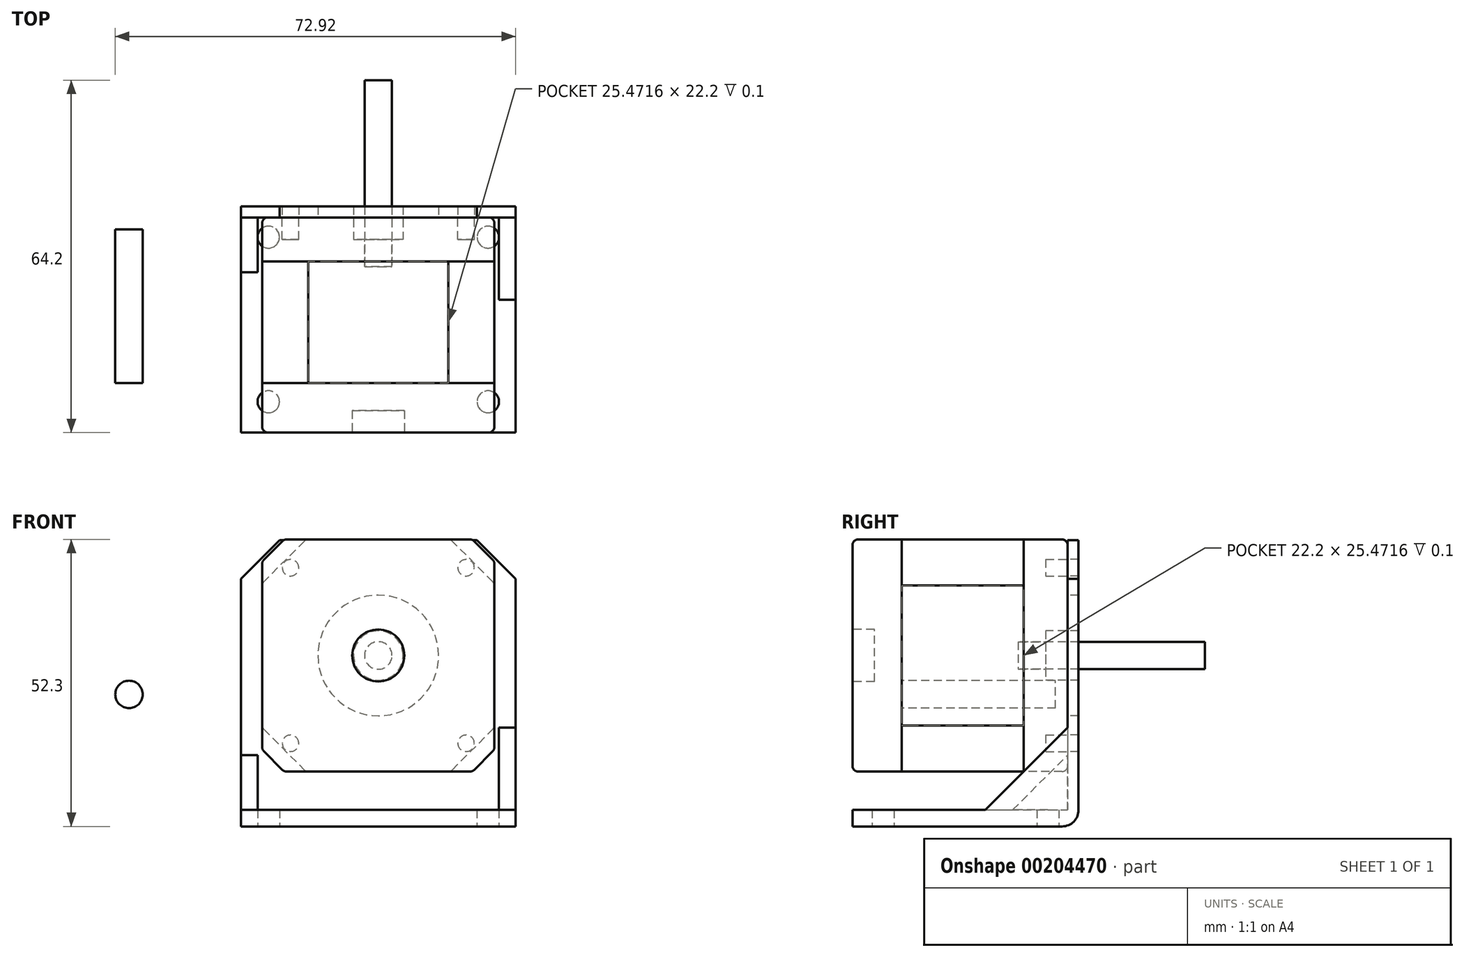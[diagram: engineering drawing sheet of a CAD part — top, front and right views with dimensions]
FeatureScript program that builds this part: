
annotation { "Feature Type Name" : "Feature", "Feature Type Description" : "" }
export const myFeature = defineFeature(function(context is Context, id is Id, definition is map)
    precondition{}
    {
        {
            var Q0;
            Q0=qCreatedBy(makeId("Front.planeOp"),FACE);
            var sketch = newSketch(context, id + "F0", { "sketchPlane" : qUnion([Q0])});
            skLineSegment(sketch, "E0.bottom", {"start": v(-21.15, 21.15) * mm, "end": v(21.15, 21.15) * mm});
            skLineSegment(sketch, "E0.top", {"start": v(-21.15, -21.15) * mm, "end": v(21.15, -21.15) * mm});
            skLineSegment(sketch, "E0.left", {"start": v(-21.15, 21.15) * mm, "end": v(-21.15, -21.15) * mm});
            skLineSegment(sketch, "E0.right", {"start": v(21.15, 21.15) * mm, "end": v(21.15, -21.15) * mm});
            skSolve(sketch);
        }
        {
            var Q0;
            Q0=makeQuery(id+"F0.imprint","IMPRINT",FACE,{"disambiguationData":[TD([[makeQuery(id+"F0.imprint","IMPRINT",EDGE,{"derivedFrom":sQuery(id+"F0.wireOp",EDGE,"E0.bottom")}),-1.0]])]});
            extrude(context, id + "F1", {"entities" : qUnion([Q0]), "depth" : 9 * mm});
        }
        {
            var Q0;
            Q0=makeQuery(id+"F1.opExtrude","CAP_FACE",FACE,{"disambiguationData":[OSD([sQuery(id+"F0.wireOp",EDGE,"E0.bottom"),sQuery(id+"F0.wireOp",EDGE,"E0.top"),sQuery(id+"F0.wireOp",EDGE,"E0.left"),sQuery(id+"F0.wireOp",EDGE,"E0.right")])],"isStart":true});
            var sketch = newSketch(context, id + "F2", { "sketchPlane" : qUnion([Q0])});
            skLineSegment(sketch, "E1.bottom", {"start": v(-21.15, 21.15) * mm, "end": v(21.15, 21.15) * mm});
            skLineSegment(sketch, "E1.top", {"start": v(-21.15, -21.15) * mm, "end": v(21.15, -21.15) * mm});
            skLineSegment(sketch, "E1.left", {"start": v(-21.15, 21.15) * mm, "end": v(-21.15, -21.15) * mm});
            skLineSegment(sketch, "E1.right", {"start": v(21.15, 21.15) * mm, "end": v(21.15, -21.15) * mm});
            skPoint(sketch, "E2", {"position": v(-13.15, 21.15) * mm});
            skPoint(sketch, "E3", {"position": v(-21.15, 13.15) * mm});
            skLineSegment(sketch, "E4", {"start": v(-21.15, 13.15) * mm, "end": v(-13.15, 21.15) * mm});
            skLineSegment(sketch, "E5.1.0", {"start": v(-13.15, -21.15) * mm, "end": v(-21.15, -13.15) * mm});
            skLineSegment(sketch, "E5.2.0", {"start": v(21.15, -13.15) * mm, "end": v(13.15, -21.15) * mm});
            skLineSegment(sketch, "E5.3.0", {"start": v(13.15, 21.15) * mm, "end": v(21.15, 13.15) * mm});
            skPoint(sketch, "E5.center", {"position": v(0, 0) * mm});
            skSolve(sketch);
        }
        {
            var Q0;
            Q0=makeQuery(id+"F1.opExtrude","SWEPT_EDGE",EDGE,{"disambiguationData":[OSD([sQuery(id+"F0.wireOp",EDGE,"E0.bottom"),sQuery(id+"F0.wireOp",EDGE,"E0.right")])]});
            var Q1;
            Q1=makeQuery(id+"F1.opExtrude","SWEPT_EDGE",EDGE,{"disambiguationData":[OSD([sQuery(id+"F0.wireOp",EDGE,"E0.bottom"),sQuery(id+"F0.wireOp",EDGE,"E0.left")])]});
            var Q2;
            Q2=makeQuery(id+"F1.opExtrude","SWEPT_EDGE",EDGE,{"disambiguationData":[OSD([sQuery(id+"F0.wireOp",EDGE,"E0.top"),sQuery(id+"F0.wireOp",EDGE,"E0.right")])]});
            var Q3;
            Q3=makeQuery(id+"F1.opExtrude","SWEPT_EDGE",EDGE,{"disambiguationData":[OSD([sQuery(id+"F0.wireOp",EDGE,"E0.top"),sQuery(id+"F0.wireOp",EDGE,"E0.left")])]});
            chamfer(context, id + "F3", {"entities" : qUnion([Q0, Q1, Q2, Q3]), "width" : 4 * mm, "tangentPropagation" : true});
        }
        {
            var Q0;
            {var subQ0=sQuery(id+"F0.wireOp",EDGE,"E0.bottom");Q0=makeQuery(id+"F3.opChamfer","BLEND_EDGE",EDGE,{"blendedFrom":[makeQuery(id+"F1.opExtrude","SWEPT_EDGE",EDGE,{"disambiguationData":[OSD([subQ0,sQuery(id+"F0.wireOp",EDGE,"E0.right")])]}),makeQuery(id+"F1.opExtrude","SWEPT_FACE",FACE,{"disambiguationData":[OSD([subQ0])]})],"blendedInto":[makeQuery(id+"F1.opExtrude","SWEPT_FACE",FACE,{"disambiguationData":[OSD([subQ0])]})]});}
            var Q1;
            {var subQ0=sQuery(id+"F0.wireOp",EDGE,"E0.right");Q1=makeQuery(id+"F3.opChamfer","BLEND_EDGE",EDGE,{"blendedFrom":[makeQuery(id+"F1.opExtrude","SWEPT_EDGE",EDGE,{"disambiguationData":[OSD([sQuery(id+"F0.wireOp",EDGE,"E0.bottom"),subQ0])]}),makeQuery(id+"F1.opExtrude","SWEPT_FACE",FACE,{"disambiguationData":[OSD([subQ0])]})],"blendedInto":[makeQuery(id+"F1.opExtrude","SWEPT_FACE",FACE,{"disambiguationData":[OSD([subQ0])]})]});}
            var Q2;
            {var subQ0=sQuery(id+"F0.wireOp",EDGE,"E0.bottom");Q2=makeQuery(id+"F3.opChamfer","BLEND_EDGE",EDGE,{"blendedFrom":[makeQuery(id+"F1.opExtrude","SWEPT_EDGE",EDGE,{"disambiguationData":[OSD([subQ0,sQuery(id+"F0.wireOp",EDGE,"E0.left")])]}),makeQuery(id+"F1.opExtrude","SWEPT_FACE",FACE,{"disambiguationData":[OSD([subQ0])]})],"blendedInto":[makeQuery(id+"F1.opExtrude","SWEPT_FACE",FACE,{"disambiguationData":[OSD([subQ0])]})]});}
            var Q3;
            {var subQ0=sQuery(id+"F0.wireOp",EDGE,"E0.right");Q3=makeQuery(id+"F3.opChamfer","BLEND_EDGE",EDGE,{"blendedFrom":[makeQuery(id+"F1.opExtrude","SWEPT_EDGE",EDGE,{"disambiguationData":[OSD([sQuery(id+"F0.wireOp",EDGE,"E0.top"),subQ0])]}),makeQuery(id+"F1.opExtrude","SWEPT_FACE",FACE,{"disambiguationData":[OSD([subQ0])]})],"blendedInto":[makeQuery(id+"F1.opExtrude","SWEPT_FACE",FACE,{"disambiguationData":[OSD([subQ0])]})]});}
            var Q4;
            {var subQ0=sQuery(id+"F0.wireOp",EDGE,"E0.top");Q4=makeQuery(id+"F3.opChamfer","BLEND_EDGE",EDGE,{"blendedFrom":[makeQuery(id+"F1.opExtrude","SWEPT_EDGE",EDGE,{"disambiguationData":[OSD([subQ0,sQuery(id+"F0.wireOp",EDGE,"E0.right")])]}),makeQuery(id+"F1.opExtrude","SWEPT_FACE",FACE,{"disambiguationData":[OSD([subQ0])]})],"blendedInto":[makeQuery(id+"F1.opExtrude","SWEPT_FACE",FACE,{"disambiguationData":[OSD([subQ0])]})]});}
            var Q5;
            {var subQ0=sQuery(id+"F0.wireOp",EDGE,"E0.left");Q5=makeQuery(id+"F3.opChamfer","BLEND_EDGE",EDGE,{"blendedFrom":[makeQuery(id+"F1.opExtrude","SWEPT_EDGE",EDGE,{"disambiguationData":[OSD([sQuery(id+"F0.wireOp",EDGE,"E0.bottom"),subQ0])]}),makeQuery(id+"F1.opExtrude","SWEPT_FACE",FACE,{"disambiguationData":[OSD([subQ0])]})],"blendedInto":[makeQuery(id+"F1.opExtrude","SWEPT_FACE",FACE,{"disambiguationData":[OSD([subQ0])]})]});}
            var Q6;
            {var subQ0=sQuery(id+"F0.wireOp",EDGE,"E0.left");Q6=makeQuery(id+"F3.opChamfer","BLEND_EDGE",EDGE,{"blendedFrom":[makeQuery(id+"F1.opExtrude","SWEPT_EDGE",EDGE,{"disambiguationData":[OSD([sQuery(id+"F0.wireOp",EDGE,"E0.top"),subQ0])]}),makeQuery(id+"F1.opExtrude","SWEPT_FACE",FACE,{"disambiguationData":[OSD([subQ0])]})],"blendedInto":[makeQuery(id+"F1.opExtrude","SWEPT_FACE",FACE,{"disambiguationData":[OSD([subQ0])]})]});}
            var Q7;
            {var subQ0=sQuery(id+"F0.wireOp",EDGE,"E0.top");Q7=makeQuery(id+"F3.opChamfer","BLEND_EDGE",EDGE,{"blendedFrom":[makeQuery(id+"F1.opExtrude","SWEPT_EDGE",EDGE,{"disambiguationData":[OSD([subQ0,sQuery(id+"F0.wireOp",EDGE,"E0.left")])]}),makeQuery(id+"F1.opExtrude","SWEPT_FACE",FACE,{"disambiguationData":[OSD([subQ0])]})],"blendedInto":[makeQuery(id+"F1.opExtrude","SWEPT_FACE",FACE,{"disambiguationData":[OSD([subQ0])]})]});}
            fillet(context, id + "F4", {"entities" : qUnion([Q0, Q1, Q2, Q3, Q4, Q5, Q6, Q7]), "radius" : 1 * mm, "tangentPropagation" : true, "allowEdgeOverflow" : false});
        }
        {
            var Q0;
            {var subQ0=sQuery(id+"F2.wireOp",EDGE,"E4");Q0=makeQuery(id+"F2.imprint","IMPRINT",FACE,{"disambiguationData":[TD([[makeQuery(id+"F2.imprint","IMPRINT",EDGE,{"derivedFrom":subQ0}),-1.0]])]});}
            extrude(context, id + "F5", {"entities" : qUnion([Q0]), "operationType" : NewBodyOperationType.ADD, "depth" : 22.2 * mm});
        }
        {
            var Q0;
            Q0=makeQuery(id+"F5.opExtrude","CAP_FACE",FACE,{"disambiguationData":[OSD([sQuery(id+"F2.wireOp",EDGE,"E1.bottom"),sQuery(id+"F2.wireOp",EDGE,"E1.top"),sQuery(id+"F2.wireOp",EDGE,"E1.left"),sQuery(id+"F2.wireOp",EDGE,"E1.right"),sQuery(id+"F2.wireOp",EDGE,"E4"),sQuery(id+"F2.wireOp",EDGE,"E5.1.0"),sQuery(id+"F2.wireOp",EDGE,"E5.2.0"),sQuery(id+"F2.wireOp",EDGE,"E5.3.0")])],"isStart":false});
            var sketch = newSketch(context, id + "F6", { "sketchPlane" : qUnion([Q0])});
            skLineSegment(sketch, "E6.bottom", {"start": v(-21.15, 21.15) * mm, "end": v(21.15, 21.15) * mm});
            skLineSegment(sketch, "E6.top", {"start": v(-21.15, -21.15) * mm, "end": v(21.15, -21.15) * mm});
            skLineSegment(sketch, "E6.left", {"start": v(-21.15, 21.15) * mm, "end": v(-21.15, -21.15) * mm});
            skLineSegment(sketch, "E6.right", {"start": v(21.15, 21.15) * mm, "end": v(21.15, -21.15) * mm});
            skSolve(sketch);
        }
        {
            var Q0;
            Q0=qSketchRegion(id+"F6",true);
            extrude(context, id + "F7", {"entities" : qUnion([Q0]), "operationType" : NewBodyOperationType.ADD, "depth" : 8 * mm});
        }
        {
            var Q0;
            Q0=makeQuery(id+"F7.opExtrude","SWEPT_EDGE",EDGE,{"disambiguationData":[OSD([sQuery(id+"F6.wireOp",EDGE,"E6.bottom"),sQuery(id+"F6.wireOp",EDGE,"E6.left")])]});
            var Q1;
            Q1=makeQuery(id+"F7.opExtrude","SWEPT_EDGE",EDGE,{"disambiguationData":[OSD([sQuery(id+"F6.wireOp",EDGE,"E6.bottom"),sQuery(id+"F6.wireOp",EDGE,"E6.right")])]});
            var Q2;
            Q2=makeQuery(id+"F7.opExtrude","SWEPT_EDGE",EDGE,{"disambiguationData":[OSD([sQuery(id+"F6.wireOp",EDGE,"E6.top"),sQuery(id+"F6.wireOp",EDGE,"E6.left")])]});
            var Q3;
            Q3=makeQuery(id+"F7.opExtrude","SWEPT_EDGE",EDGE,{"disambiguationData":[OSD([sQuery(id+"F6.wireOp",EDGE,"E6.top"),sQuery(id+"F6.wireOp",EDGE,"E6.right")])]});
            chamfer(context, id + "F8", {"entities" : qUnion([Q0, Q1, Q2, Q3]), "width" : 4 * mm, "tangentPropagation" : true});
        }
        {
            var Q0;
            Q0=makeQuery(id+"F1.opExtrude","CAP_EDGE",EDGE,{"disambiguationData":[OSD([sQuery(id+"F0.wireOp",EDGE,"E0.right")])],"isStart":false});
            var Q1;
            Q1=makeQuery(id+"F5.opExtrude","SWEPT_EDGE",EDGE,{"disambiguationData":[OSD([sQuery(id+"F2.wireOp",EDGE,"E1.left"),sQuery(id+"F2.wireOp",EDGE,"E4")])]});
            var Q2;
            Q2=makeQuery(id+"F5.opExtrude","SWEPT_EDGE",EDGE,{"disambiguationData":[OSD([sQuery(id+"F2.wireOp",EDGE,"E1.bottom"),sQuery(id+"F2.wireOp",EDGE,"E4")])]});
            var Q3;
            {var subQ0=sQuery(id+"F6.wireOp",EDGE,"E6.left");Q3=makeQuery(id+"F8.opChamfer","BLEND_EDGE",EDGE,{"blendedFrom":[makeQuery(id+"F7.opExtrude","SWEPT_EDGE",EDGE,{"disambiguationData":[OSD([sQuery(id+"F6.wireOp",EDGE,"E6.bottom"),subQ0])]}),makeQuery(id+"F7.boolean.opBoolean","MERGE",FACE,{"derivedFrom":[makeQuery(id+"F5.boolean.opBoolean","MERGE",FACE,{"derivedFrom":[makeQuery(id+"F1.opExtrude","SWEPT_FACE",FACE,{"disambiguationData":[OSD([sQuery(id+"F0.wireOp",EDGE,"E0.right")])]}),makeQuery(id+"F5.opExtrude","SWEPT_FACE",FACE,{"disambiguationData":[OSD([sQuery(id+"F2.wireOp",EDGE,"E1.left")])]})]}),makeQuery(id+"F7.opExtrude","SWEPT_FACE",FACE,{"disambiguationData":[OSD([subQ0])]})]})],"blendedInto":[makeQuery(id+"F7.boolean.opBoolean","MERGE",FACE,{"derivedFrom":[makeQuery(id+"F5.boolean.opBoolean","MERGE",FACE,{"derivedFrom":[makeQuery(id+"F1.opExtrude","SWEPT_FACE",FACE,{"disambiguationData":[OSD([sQuery(id+"F0.wireOp",EDGE,"E0.right")])]}),makeQuery(id+"F5.opExtrude","SWEPT_FACE",FACE,{"disambiguationData":[OSD([sQuery(id+"F2.wireOp",EDGE,"E1.left")])]})]}),makeQuery(id+"F7.opExtrude","SWEPT_FACE",FACE,{"disambiguationData":[OSD([subQ0])]})]})]});}
            var Q4;
            {var subQ0=sQuery(id+"F6.wireOp",EDGE,"E6.bottom");Q4=makeQuery(id+"F8.opChamfer","BLEND_EDGE",EDGE,{"blendedFrom":[makeQuery(id+"F7.opExtrude","SWEPT_EDGE",EDGE,{"disambiguationData":[OSD([subQ0,sQuery(id+"F6.wireOp",EDGE,"E6.left")])]}),makeQuery(id+"F7.boolean.opBoolean","MERGE",FACE,{"derivedFrom":[makeQuery(id+"F5.boolean.opBoolean","MERGE",FACE,{"derivedFrom":[makeQuery(id+"F1.opExtrude","SWEPT_FACE",FACE,{"disambiguationData":[OSD([sQuery(id+"F0.wireOp",EDGE,"E0.bottom")])]}),makeQuery(id+"F5.opExtrude","SWEPT_FACE",FACE,{"disambiguationData":[OSD([sQuery(id+"F2.wireOp",EDGE,"E1.bottom")])]})]}),makeQuery(id+"F7.opExtrude","SWEPT_FACE",FACE,{"disambiguationData":[OSD([subQ0])]})]})],"blendedInto":[makeQuery(id+"F7.boolean.opBoolean","MERGE",FACE,{"derivedFrom":[makeQuery(id+"F5.boolean.opBoolean","MERGE",FACE,{"derivedFrom":[makeQuery(id+"F1.opExtrude","SWEPT_FACE",FACE,{"disambiguationData":[OSD([sQuery(id+"F0.wireOp",EDGE,"E0.bottom")])]}),makeQuery(id+"F5.opExtrude","SWEPT_FACE",FACE,{"disambiguationData":[OSD([sQuery(id+"F2.wireOp",EDGE,"E1.bottom")])]})]}),makeQuery(id+"F7.opExtrude","SWEPT_FACE",FACE,{"disambiguationData":[OSD([subQ0])]})]})]});}
            var Q5;
            {var subQ0=sQuery(id+"F6.wireOp",EDGE,"E6.bottom");Q5=makeQuery(id+"F8.opChamfer","BLEND_EDGE",EDGE,{"blendedFrom":[makeQuery(id+"F7.opExtrude","SWEPT_EDGE",EDGE,{"disambiguationData":[OSD([subQ0,sQuery(id+"F6.wireOp",EDGE,"E6.right")])]}),makeQuery(id+"F7.boolean.opBoolean","MERGE",FACE,{"derivedFrom":[makeQuery(id+"F5.boolean.opBoolean","MERGE",FACE,{"derivedFrom":[makeQuery(id+"F1.opExtrude","SWEPT_FACE",FACE,{"disambiguationData":[OSD([sQuery(id+"F0.wireOp",EDGE,"E0.bottom")])]}),makeQuery(id+"F5.opExtrude","SWEPT_FACE",FACE,{"disambiguationData":[OSD([sQuery(id+"F2.wireOp",EDGE,"E1.bottom")])]})]}),makeQuery(id+"F7.opExtrude","SWEPT_FACE",FACE,{"disambiguationData":[OSD([subQ0])]})]})],"blendedInto":[makeQuery(id+"F7.boolean.opBoolean","MERGE",FACE,{"derivedFrom":[makeQuery(id+"F5.boolean.opBoolean","MERGE",FACE,{"derivedFrom":[makeQuery(id+"F1.opExtrude","SWEPT_FACE",FACE,{"disambiguationData":[OSD([sQuery(id+"F0.wireOp",EDGE,"E0.bottom")])]}),makeQuery(id+"F5.opExtrude","SWEPT_FACE",FACE,{"disambiguationData":[OSD([sQuery(id+"F2.wireOp",EDGE,"E1.bottom")])]})]}),makeQuery(id+"F7.opExtrude","SWEPT_FACE",FACE,{"disambiguationData":[OSD([subQ0])]})]})]});}
            var Q6;
            Q6=makeQuery(id+"F5.opExtrude","SWEPT_EDGE",EDGE,{"disambiguationData":[OSD([sQuery(id+"F2.wireOp",EDGE,"E1.bottom"),sQuery(id+"F2.wireOp",EDGE,"E5.3.0")])]});
            var Q7;
            {var subQ0=sQuery(id+"F6.wireOp",EDGE,"E6.right");Q7=makeQuery(id+"F8.opChamfer","BLEND_EDGE",EDGE,{"blendedFrom":[makeQuery(id+"F7.opExtrude","SWEPT_EDGE",EDGE,{"disambiguationData":[OSD([sQuery(id+"F6.wireOp",EDGE,"E6.bottom"),subQ0])]}),makeQuery(id+"F7.boolean.opBoolean","MERGE",FACE,{"derivedFrom":[makeQuery(id+"F5.boolean.opBoolean","MERGE",FACE,{"derivedFrom":[makeQuery(id+"F1.opExtrude","SWEPT_FACE",FACE,{"disambiguationData":[OSD([sQuery(id+"F0.wireOp",EDGE,"E0.left")])]}),makeQuery(id+"F5.opExtrude","SWEPT_FACE",FACE,{"disambiguationData":[OSD([sQuery(id+"F2.wireOp",EDGE,"E1.right")])]})]}),makeQuery(id+"F7.opExtrude","SWEPT_FACE",FACE,{"disambiguationData":[OSD([subQ0])]})]})],"blendedInto":[makeQuery(id+"F7.boolean.opBoolean","MERGE",FACE,{"derivedFrom":[makeQuery(id+"F5.boolean.opBoolean","MERGE",FACE,{"derivedFrom":[makeQuery(id+"F1.opExtrude","SWEPT_FACE",FACE,{"disambiguationData":[OSD([sQuery(id+"F0.wireOp",EDGE,"E0.left")])]}),makeQuery(id+"F5.opExtrude","SWEPT_FACE",FACE,{"disambiguationData":[OSD([sQuery(id+"F2.wireOp",EDGE,"E1.right")])]})]}),makeQuery(id+"F7.opExtrude","SWEPT_FACE",FACE,{"disambiguationData":[OSD([subQ0])]})]})]});}
            var Q8;
            Q8=makeQuery(id+"F5.opExtrude","SWEPT_EDGE",EDGE,{"disambiguationData":[OSD([sQuery(id+"F2.wireOp",EDGE,"E1.right"),sQuery(id+"F2.wireOp",EDGE,"E5.3.0")])]});
            var Q9;
            Q9=makeQuery(id+"F5.opExtrude","SWEPT_EDGE",EDGE,{"disambiguationData":[OSD([sQuery(id+"F2.wireOp",EDGE,"E1.right"),sQuery(id+"F2.wireOp",EDGE,"E5.2.0")])]});
            var Q10;
            {var subQ0=sQuery(id+"F6.wireOp",EDGE,"E6.right");Q10=makeQuery(id+"F8.opChamfer","BLEND_EDGE",EDGE,{"blendedFrom":[makeQuery(id+"F7.opExtrude","SWEPT_EDGE",EDGE,{"disambiguationData":[OSD([sQuery(id+"F6.wireOp",EDGE,"E6.top"),subQ0])]}),makeQuery(id+"F7.boolean.opBoolean","MERGE",FACE,{"derivedFrom":[makeQuery(id+"F5.boolean.opBoolean","MERGE",FACE,{"derivedFrom":[makeQuery(id+"F1.opExtrude","SWEPT_FACE",FACE,{"disambiguationData":[OSD([sQuery(id+"F0.wireOp",EDGE,"E0.left")])]}),makeQuery(id+"F5.opExtrude","SWEPT_FACE",FACE,{"disambiguationData":[OSD([sQuery(id+"F2.wireOp",EDGE,"E1.right")])]})]}),makeQuery(id+"F7.opExtrude","SWEPT_FACE",FACE,{"disambiguationData":[OSD([subQ0])]})]})],"blendedInto":[makeQuery(id+"F7.boolean.opBoolean","MERGE",FACE,{"derivedFrom":[makeQuery(id+"F5.boolean.opBoolean","MERGE",FACE,{"derivedFrom":[makeQuery(id+"F1.opExtrude","SWEPT_FACE",FACE,{"disambiguationData":[OSD([sQuery(id+"F0.wireOp",EDGE,"E0.left")])]}),makeQuery(id+"F5.opExtrude","SWEPT_FACE",FACE,{"disambiguationData":[OSD([sQuery(id+"F2.wireOp",EDGE,"E1.right")])]})]}),makeQuery(id+"F7.opExtrude","SWEPT_FACE",FACE,{"disambiguationData":[OSD([subQ0])]})]})]});}
            var Q11;
            {var subQ0=sQuery(id+"F6.wireOp",EDGE,"E6.top");Q11=makeQuery(id+"F8.opChamfer","BLEND_EDGE",EDGE,{"blendedFrom":[makeQuery(id+"F7.opExtrude","SWEPT_EDGE",EDGE,{"disambiguationData":[OSD([subQ0,sQuery(id+"F6.wireOp",EDGE,"E6.right")])]}),makeQuery(id+"F7.boolean.opBoolean","MERGE",FACE,{"derivedFrom":[makeQuery(id+"F5.boolean.opBoolean","MERGE",FACE,{"derivedFrom":[makeQuery(id+"F1.opExtrude","SWEPT_FACE",FACE,{"disambiguationData":[OSD([sQuery(id+"F0.wireOp",EDGE,"E0.top")])]}),makeQuery(id+"F5.opExtrude","SWEPT_FACE",FACE,{"disambiguationData":[OSD([sQuery(id+"F2.wireOp",EDGE,"E1.top")])]})]}),makeQuery(id+"F7.opExtrude","SWEPT_FACE",FACE,{"disambiguationData":[OSD([subQ0])]})]})],"blendedInto":[makeQuery(id+"F7.boolean.opBoolean","MERGE",FACE,{"derivedFrom":[makeQuery(id+"F5.boolean.opBoolean","MERGE",FACE,{"derivedFrom":[makeQuery(id+"F1.opExtrude","SWEPT_FACE",FACE,{"disambiguationData":[OSD([sQuery(id+"F0.wireOp",EDGE,"E0.top")])]}),makeQuery(id+"F5.opExtrude","SWEPT_FACE",FACE,{"disambiguationData":[OSD([sQuery(id+"F2.wireOp",EDGE,"E1.top")])]})]}),makeQuery(id+"F7.opExtrude","SWEPT_FACE",FACE,{"disambiguationData":[OSD([subQ0])]})]})]});}
            var Q12;
            Q12=makeQuery(id+"F5.opExtrude","SWEPT_EDGE",EDGE,{"disambiguationData":[OSD([sQuery(id+"F2.wireOp",EDGE,"E1.top"),sQuery(id+"F2.wireOp",EDGE,"E5.2.0")])]});
            var Q13;
            Q13=makeQuery(id+"F5.opExtrude","SWEPT_EDGE",EDGE,{"disambiguationData":[OSD([sQuery(id+"F2.wireOp",EDGE,"E1.top"),sQuery(id+"F2.wireOp",EDGE,"E5.1.0")])]});
            var Q14;
            {var subQ0=sQuery(id+"F6.wireOp",EDGE,"E6.top");Q14=makeQuery(id+"F8.opChamfer","BLEND_EDGE",EDGE,{"blendedFrom":[makeQuery(id+"F7.opExtrude","SWEPT_EDGE",EDGE,{"disambiguationData":[OSD([subQ0,sQuery(id+"F6.wireOp",EDGE,"E6.left")])]}),makeQuery(id+"F7.boolean.opBoolean","MERGE",FACE,{"derivedFrom":[makeQuery(id+"F5.boolean.opBoolean","MERGE",FACE,{"derivedFrom":[makeQuery(id+"F1.opExtrude","SWEPT_FACE",FACE,{"disambiguationData":[OSD([sQuery(id+"F0.wireOp",EDGE,"E0.top")])]}),makeQuery(id+"F5.opExtrude","SWEPT_FACE",FACE,{"disambiguationData":[OSD([sQuery(id+"F2.wireOp",EDGE,"E1.top")])]})]}),makeQuery(id+"F7.opExtrude","SWEPT_FACE",FACE,{"disambiguationData":[OSD([subQ0])]})]})],"blendedInto":[makeQuery(id+"F7.boolean.opBoolean","MERGE",FACE,{"derivedFrom":[makeQuery(id+"F5.boolean.opBoolean","MERGE",FACE,{"derivedFrom":[makeQuery(id+"F1.opExtrude","SWEPT_FACE",FACE,{"disambiguationData":[OSD([sQuery(id+"F0.wireOp",EDGE,"E0.top")])]}),makeQuery(id+"F5.opExtrude","SWEPT_FACE",FACE,{"disambiguationData":[OSD([sQuery(id+"F2.wireOp",EDGE,"E1.top")])]})]}),makeQuery(id+"F7.opExtrude","SWEPT_FACE",FACE,{"disambiguationData":[OSD([subQ0])]})]})]});}
            var Q15;
            {var subQ0=sQuery(id+"F6.wireOp",EDGE,"E6.left");Q15=makeQuery(id+"F8.opChamfer","BLEND_EDGE",EDGE,{"blendedFrom":[makeQuery(id+"F7.opExtrude","SWEPT_EDGE",EDGE,{"disambiguationData":[OSD([sQuery(id+"F6.wireOp",EDGE,"E6.top"),subQ0])]}),makeQuery(id+"F7.boolean.opBoolean","MERGE",FACE,{"derivedFrom":[makeQuery(id+"F5.boolean.opBoolean","MERGE",FACE,{"derivedFrom":[makeQuery(id+"F1.opExtrude","SWEPT_FACE",FACE,{"disambiguationData":[OSD([sQuery(id+"F0.wireOp",EDGE,"E0.right")])]}),makeQuery(id+"F5.opExtrude","SWEPT_FACE",FACE,{"disambiguationData":[OSD([sQuery(id+"F2.wireOp",EDGE,"E1.left")])]})]}),makeQuery(id+"F7.opExtrude","SWEPT_FACE",FACE,{"disambiguationData":[OSD([subQ0])]})]})],"blendedInto":[makeQuery(id+"F7.boolean.opBoolean","MERGE",FACE,{"derivedFrom":[makeQuery(id+"F5.boolean.opBoolean","MERGE",FACE,{"derivedFrom":[makeQuery(id+"F1.opExtrude","SWEPT_FACE",FACE,{"disambiguationData":[OSD([sQuery(id+"F0.wireOp",EDGE,"E0.right")])]}),makeQuery(id+"F5.opExtrude","SWEPT_FACE",FACE,{"disambiguationData":[OSD([sQuery(id+"F2.wireOp",EDGE,"E1.left")])]})]}),makeQuery(id+"F7.opExtrude","SWEPT_FACE",FACE,{"disambiguationData":[OSD([subQ0])]})]})]});}
            var Q16;
            Q16=makeQuery(id+"F5.opExtrude","SWEPT_EDGE",EDGE,{"disambiguationData":[OSD([sQuery(id+"F2.wireOp",EDGE,"E1.left"),sQuery(id+"F2.wireOp",EDGE,"E5.1.0")])]});
            var Q17;
            Q17=makeQuery(id+"F7.opExtrude","CAP_EDGE",EDGE,{"disambiguationData":[OSD([sQuery(id+"F6.wireOp",EDGE,"E6.bottom")])],"isStart":false});
            var Q18;
            Q18=makeQuery(id+"F7.opExtrude","CAP_FACE",FACE,{"disambiguationData":[OSD([sQuery(id+"F6.wireOp",EDGE,"E6.bottom"),sQuery(id+"F6.wireOp",EDGE,"E6.top"),sQuery(id+"F6.wireOp",EDGE,"E6.left"),sQuery(id+"F6.wireOp",EDGE,"E6.right")])],"isStart":false});
            fillet(context, id + "F9", {"entities" : qUnion([Q0, Q1, Q2, Q3, Q4, Q5, Q6, Q7, Q8, Q9, Q10, Q11, Q12, Q13, Q14, Q15, Q16, Q17, Q18]), "radius" : 1 * mm, "tangentPropagation" : true, "allowEdgeOverflow" : false});
        }
        {
            var Q0;
            Q0=makeQuery(id+"F7.boolean.opBoolean","MERGE",FACE,{"derivedFrom":[makeQuery(id+"F5.boolean.opBoolean","MERGE",FACE,{"derivedFrom":[makeQuery(id+"F1.opExtrude","SWEPT_FACE",FACE,{"disambiguationData":[OSD([sQuery(id+"F0.wireOp",EDGE,"E0.right")])]}),makeQuery(id+"F5.opExtrude","SWEPT_FACE",FACE,{"disambiguationData":[OSD([sQuery(id+"F2.wireOp",EDGE,"E1.left")])]})]}),makeQuery(id+"F7.opExtrude","SWEPT_FACE",FACE,{"disambiguationData":[OSD([sQuery(id+"F6.wireOp",EDGE,"E6.left")])]})]});
            var sketch = newSketch(context, id + "F10", { "sketchPlane" : qUnion([Q0])});
            skLineSegment(sketch, "E7", {"start": v(0, 12.74) * mm, "end": v(0, -12.74) * mm});
            skLineSegment(sketch, "E8", {"start": v(22.2, 12.74) * mm, "end": v(22.2, -12.74) * mm});
            skSolve(sketch);
        }
        {
            var Q0;
            Q0=makeQuery(id+"F10.imprint","IMPRINT",FACE,{"disambiguationData":[TD([[makeQuery(id+"F10.imprint","IMPRINT",EDGE,{"derivedFrom":sQuery(id+"F10.wireOp",EDGE,"E7")}),1.0]])]});
            extrude(context, id + "F11", {"entities" : qUnion([Q0]), "operationType" : NewBodyOperationType.REMOVE, "oppositeDirection" : true, "depth" : 0.1 * mm});
        }
        {
            var Q0;
            Q0=makeQuery(id+"F7.boolean.opBoolean","MERGE",FACE,{"derivedFrom":[makeQuery(id+"F5.boolean.opBoolean","MERGE",FACE,{"derivedFrom":[makeQuery(id+"F1.opExtrude","SWEPT_FACE",FACE,{"disambiguationData":[OSD([sQuery(id+"F0.wireOp",EDGE,"E0.bottom")])]}),makeQuery(id+"F5.opExtrude","SWEPT_FACE",FACE,{"disambiguationData":[OSD([sQuery(id+"F2.wireOp",EDGE,"E1.bottom")])]})]}),makeQuery(id+"F7.opExtrude","SWEPT_FACE",FACE,{"disambiguationData":[OSD([sQuery(id+"F6.wireOp",EDGE,"E6.bottom")])]})]});
            var sketch = newSketch(context, id + "F12", { "sketchPlane" : qUnion([Q0])});
            skLineSegment(sketch, "E9", {"start": v(12.74, 0) * mm, "end": v(-12.74, 0) * mm});
            skLineSegment(sketch, "E10", {"start": v(-12.74, 22.2) * mm, "end": v(12.74, 22.2) * mm});
            skSolve(sketch);
        }
        {
            var Q0;
            Q0=makeQuery(id+"F12.imprint","IMPRINT",FACE,{"disambiguationData":[TD([[makeQuery(id+"F12.imprint","IMPRINT",EDGE,{"derivedFrom":sQuery(id+"F12.wireOp",EDGE,"E9")}),-1.0]])]});
            extrude(context, id + "F13", {"entities" : qUnion([Q0]), "operationType" : NewBodyOperationType.REMOVE, "oppositeDirection" : true, "depth" : 0.1 * mm});
        }
        {
            var Q0;
            Q0=makeQuery(id+"F7.boolean.opBoolean","MERGE",FACE,{"derivedFrom":[makeQuery(id+"F5.boolean.opBoolean","MERGE",FACE,{"derivedFrom":[makeQuery(id+"F1.opExtrude","SWEPT_FACE",FACE,{"disambiguationData":[OSD([sQuery(id+"F0.wireOp",EDGE,"E0.left")])]}),makeQuery(id+"F5.opExtrude","SWEPT_FACE",FACE,{"disambiguationData":[OSD([sQuery(id+"F2.wireOp",EDGE,"E1.right")])]})]}),makeQuery(id+"F7.opExtrude","SWEPT_FACE",FACE,{"disambiguationData":[OSD([sQuery(id+"F6.wireOp",EDGE,"E6.right")])]})]});
            var sketch = newSketch(context, id + "F14", { "sketchPlane" : qUnion([Q0])});
            skLineSegment(sketch, "E11", {"start": v(0, 12.74) * mm, "end": v(0, -12.74) * mm});
            skLineSegment(sketch, "E12", {"start": v(-22.2, 12.74) * mm, "end": v(-22.2, -12.74) * mm});
            skSolve(sketch);
        }
        {
            var Q0;
            Q0=makeQuery(id+"F14.imprint","IMPRINT",FACE,{"disambiguationData":[TD([[makeQuery(id+"F14.imprint","IMPRINT",EDGE,{"derivedFrom":sQuery(id+"F14.wireOp",EDGE,"E11")}),-1.0]])]});
            extrude(context, id + "F15", {"entities" : qUnion([Q0]), "operationType" : NewBodyOperationType.REMOVE, "oppositeDirection" : true, "depth" : 0.1 * mm});
        }
        {
            var Q0;
            Q0=makeQuery(id+"F7.boolean.opBoolean","MERGE",FACE,{"derivedFrom":[makeQuery(id+"F5.boolean.opBoolean","MERGE",FACE,{"derivedFrom":[makeQuery(id+"F1.opExtrude","SWEPT_FACE",FACE,{"disambiguationData":[OSD([sQuery(id+"F0.wireOp",EDGE,"E0.top")])]}),makeQuery(id+"F5.opExtrude","SWEPT_FACE",FACE,{"disambiguationData":[OSD([sQuery(id+"F2.wireOp",EDGE,"E1.top")])]})]}),makeQuery(id+"F7.opExtrude","SWEPT_FACE",FACE,{"disambiguationData":[OSD([sQuery(id+"F6.wireOp",EDGE,"E6.top")])]})]});
            var sketch = newSketch(context, id + "F16", { "sketchPlane" : qUnion([Q0])});
            skLineSegment(sketch, "E13", {"start": v(-12.74, 0) * mm, "end": v(12.74, 0) * mm});
            skLineSegment(sketch, "E14", {"start": v(-12.74, -22.2) * mm, "end": v(12.74, -22.2) * mm});
            skSolve(sketch);
        }
        {
            var Q0;
            Q0=makeQuery(id+"F16.imprint","IMPRINT",FACE,{"disambiguationData":[TD([[makeQuery(id+"F16.imprint","IMPRINT",EDGE,{"derivedFrom":sQuery(id+"F16.wireOp",EDGE,"E13")}),-1.0]])]});
            extrude(context, id + "F17", {"entities" : qUnion([Q0]), "operationType" : NewBodyOperationType.REMOVE, "oppositeDirection" : true, "depth" : 0.1 * mm});
        }
        {
            var Q0;
            Q0=makeQuery(id+"F7.opExtrude","CAP_FACE",FACE,{"disambiguationData":[OSD([sQuery(id+"F6.wireOp",EDGE,"E6.bottom"),sQuery(id+"F6.wireOp",EDGE,"E6.top"),sQuery(id+"F6.wireOp",EDGE,"E6.left"),sQuery(id+"F6.wireOp",EDGE,"E6.right")])],"isStart":false});
            var sketch = newSketch(context, id + "F18", { "sketchPlane" : qUnion([Q0])});
            skCircle(sketch, "E15", {"center": v(0, 0) * mm, "radius": 11 * mm});
            skCircle(sketch, "E16", {"center": v(0, 0) * mm, "radius": 4.5 * mm});
            skSolve(sketch);
        }
        {
            var Q0;
            Q0=makeQuery(id+"F18.imprint","IMPRINT",FACE,{"disambiguationData":[TD([[makeQuery(id+"F18.imprint","IMPRINT",EDGE,{"derivedFrom":sQuery(id+"F18.wireOp",EDGE,"E15")}),1.0]])]});
            extrude(context, id + "F19", {"entities" : qUnion([Q0]), "operationType" : NewBodyOperationType.ADD, "depth" : 2 * mm});
        }
        {
            var Q0;
            Q0=makeQuery(id+"F19.boolean.opBoolean","SPLIT",FACE,{"disambiguationData":[TD([makeQuery(id+"F19.opExtrude","SWEPT_FACE",FACE,{"disambiguationData":[OSD([sQuery(id+"F18.wireOp",EDGE,"E16")])]})])],"derivedFrom":makeQuery(id+"F7.opExtrude","CAP_FACE",FACE,{"disambiguationData":[OSD([sQuery(id+"F6.wireOp",EDGE,"E6.bottom"),sQuery(id+"F6.wireOp",EDGE,"E6.top"),sQuery(id+"F6.wireOp",EDGE,"E6.left"),sQuery(id+"F6.wireOp",EDGE,"E6.right")])],"isStart":false})});
            extrude(context, id + "F20", {"entities" : qUnion([Q0]), "operationType" : NewBodyOperationType.REMOVE, "oppositeDirection" : true, "depth" : 4 * mm});
        }
        {
            var Q0;
            Q0=makeQuery(id+"F20.boolean.opBoolean","COPY",FACE,{"derivedFrom":makeQuery(id+"F20.opExtrude","CAP_FACE",FACE,{"disambiguationData":[OSD([sQuery(id+"F6.wireOp",EDGE,"E6.bottom"),sQuery(id+"F6.wireOp",EDGE,"E6.top"),sQuery(id+"F6.wireOp",EDGE,"E6.left"),sQuery(id+"F6.wireOp",EDGE,"E6.right")])],"isStart":false})});
            var sketch = newSketch(context, id + "F21", { "sketchPlane" : qUnion([Q0])});
            skCircle(sketch, "E17", {"center": v(0, 0) * mm, "radius": 2.5 * mm});
            skSolve(sketch);
        }
        {
            var Q0;
            Q0=makeQuery(id+"F21.imprint","IMPRINT",FACE,{"disambiguationData":[TD([[makeQuery(id+"F21.imprint","IMPRINT",EDGE,{"derivedFrom":sQuery(id+"F21.wireOp",EDGE,"E17")}),1.0]])]});
            extrude(context, id + "F22", {"entities" : qUnion([Q0]), "operationType" : NewBodyOperationType.REMOVE, "oppositeDirection" : true, "depth" : 5 * mm});
        }
        {
            var Q0;
            {var subQ0=sQuery(id+"F6.wireOp",EDGE,"E6.right");var subQ1=sQuery(id+"F6.wireOp",EDGE,"E6.left");var subQ2=sQuery(id+"F6.wireOp",EDGE,"E6.top");var subQ3=sQuery(id+"F6.wireOp",EDGE,"E6.bottom");var subQ4=makeQuery(id+"F7.opExtrude","CAP_FACE",FACE,{"disambiguationData":[OSD([subQ3,subQ2,subQ1,subQ0])],"isStart":false});Q0=makeQuery(id+"F19.boolean.opBoolean","SPLIT",FACE,{"disambiguationData":[TD([makeQuery(id+"F9.opFillet","BLEND_FACE",FACE,{"disambiguationData":[OSD([subQ3])]})])],"derivedFrom":subQ4});}
            var sketch = newSketch(context, id + "F23", { "sketchPlane" : qUnion([Q0])});
            skCircle(sketch, "E18", {"center": v(-16, 16) * mm, "radius": 1.5 * mm});
            skCircle(sketch, "E19", {"center": v(16, 16) * mm, "radius": 1.5 * mm});
            skCircle(sketch, "E20", {"center": v(16, -16) * mm, "radius": 1.5 * mm});
            skCircle(sketch, "E21", {"center": v(-16, -16) * mm, "radius": 1.5 * mm});
            skSolve(sketch);
        }
        {
            var Q0;
            Q0=makeQuery(id+"F23.imprint","IMPRINT",FACE,{"disambiguationData":[TD([[makeQuery(id+"F23.imprint","IMPRINT",EDGE,{"derivedFrom":sQuery(id+"F23.wireOp",EDGE,"E18")}),1.0]])]});
            var Q1;
            Q1=makeQuery(id+"F23.imprint","IMPRINT",FACE,{"disambiguationData":[TD([[makeQuery(id+"F23.imprint","IMPRINT",EDGE,{"derivedFrom":sQuery(id+"F23.wireOp",EDGE,"E19")}),1.0]])]});
            var Q2;
            Q2=makeQuery(id+"F23.imprint","IMPRINT",FACE,{"disambiguationData":[TD([[makeQuery(id+"F23.imprint","IMPRINT",EDGE,{"derivedFrom":sQuery(id+"F23.wireOp",EDGE,"E21")}),1.0]])]});
            var Q3;
            Q3=makeQuery(id+"F23.imprint","IMPRINT",FACE,{"disambiguationData":[TD([[makeQuery(id+"F23.imprint","IMPRINT",EDGE,{"derivedFrom":sQuery(id+"F23.wireOp",EDGE,"E20")}),1.0]])]});
            extrude(context, id + "F24", {"entities" : qUnion([Q0, Q1, Q2, Q3]), "operationType" : NewBodyOperationType.REMOVE, "oppositeDirection" : true, "depth" : 4 * mm});
        }
        {
            var Q0;
            Q0=makeQuery(id+"F22.boolean.opBoolean","COPY",FACE,{"derivedFrom":makeQuery(id+"F22.opExtrude","CAP_FACE",FACE,{"disambiguationData":[OSD([sQuery(id+"F21.wireOp",EDGE,"E17")])],"isStart":false})});
            var sketch = newSketch(context, id + "F25", { "sketchPlane" : qUnion([Q0])});
            skCircle(sketch, "E22", {"center": v(0, 0) * mm, "radius": 2.5 * mm});
            skSolve(sketch);
        }
        {
            var Q0;
            Q0=makeQuery(id+"F25.imprint","IMPRINT",FACE,{"disambiguationData":[TD([[makeQuery(id+"F25.imprint","IMPRINT",EDGE,{"derivedFrom":sQuery(id+"F25.wireOp",EDGE,"E22")}),1.0]])]});
            extrude(context, id + "F26", {"entities" : qUnion([Q0]), "depth" : 34 * mm});
        }
        {
            var Q0;
            {var subQ0=sQuery(id+"F6.wireOp",EDGE,"E6.right");var subQ1=sQuery(id+"F6.wireOp",EDGE,"E6.left");var subQ2=sQuery(id+"F6.wireOp",EDGE,"E6.top");var subQ3=sQuery(id+"F6.wireOp",EDGE,"E6.bottom");var subQ4=makeQuery(id+"F7.opExtrude","CAP_FACE",FACE,{"disambiguationData":[OSD([subQ3,subQ2,subQ1,subQ0])],"isStart":false});Q0=makeQuery(id+"F19.boolean.opBoolean","SPLIT",FACE,{"disambiguationData":[TD([makeQuery(id+"F9.opFillet","BLEND_FACE",FACE,{"disambiguationData":[OSD([subQ3])]})])],"derivedFrom":subQ4});}
            var sketch = newSketch(context, id + "F27", { "sketchPlane" : qUnion([Q0])});
            skLineSegment(sketch, "E23.bottom", {"start": v(-25, 21) * mm, "end": v(25, 21) * mm});
            skLineSegment(sketch, "E23.top", {"start": v(-25, -31.15) * mm, "end": v(25, -31.15) * mm});
            skLineSegment(sketch, "E23.left", {"start": v(-25, 21) * mm, "end": v(-25, -31.15) * mm});
            skLineSegment(sketch, "E23.right", {"start": v(25, 21) * mm, "end": v(25, -31.15) * mm});
            skCircle(sketch, "E24", {"center": v(0, 0) * mm, "radius": 11 * mm});
            skSolve(sketch);
        }
        {
            var Q0;
            Q0=makeQuery(id+"F27.imprint","IMPRINT",FACE,{"disambiguationData":[TD([[makeQuery(id+"F27.imprint","IMPRINT",EDGE,{"derivedFrom":sQuery(id+"F27.wireOp",EDGE,"E23.bottom")}),-1.0]])]});
            var Q1;
            Q1=makeQuery(id+"F27.imprint","IMPRINT",FACE,{"disambiguationData":[TD([[makeQuery(id+"F27.imprint","IMPRINT",EDGE,{"derivedFrom":sQuery(id+"F27.wireOp",EDGE,"E24")}),-1.0]])]});
            extrude(context, id + "F28", {"entities" : qUnion([Q0, Q1]), "depth" : 2 * mm});
        }
        {
            var Q0;
            Q0=makeQuery(id+"F28.opExtrude","CAP_FACE",FACE,{"disambiguationData":[OSD([sQuery(id+"F23.wireOp",EDGE,"E18"),sQuery(id+"F23.wireOp",EDGE,"E19"),sQuery(id+"F23.wireOp",EDGE,"E20"),sQuery(id+"F23.wireOp",EDGE,"E21"),sQuery(id+"F27.wireOp",EDGE,"E23.bottom"),sQuery(id+"F27.wireOp",EDGE,"E23.top"),sQuery(id+"F27.wireOp",EDGE,"E23.left"),sQuery(id+"F27.wireOp",EDGE,"E23.right"),sQuery(id+"F27.wireOp",EDGE,"E24")])],"isStart":true});
            var sketch = newSketch(context, id + "F29", { "sketchPlane" : qUnion([Q0])});
            skLineSegment(sketch, "E25.bottom", {"start": v(-25, -31.15) * mm, "end": v(25, -31.15) * mm});
            skLineSegment(sketch, "E25.top", {"start": v(-25, -28.15) * mm, "end": v(25, -28.15) * mm});
            skLineSegment(sketch, "E25.left", {"start": v(-25, -31.15) * mm, "end": v(-25, -28.15) * mm});
            skLineSegment(sketch, "E25.right", {"start": v(25, -31.15) * mm, "end": v(25, -28.15) * mm});
            skSolve(sketch);
        }
        {
            var Q0;
            Q0=makeQuery(id+"F29.imprint","IMPRINT",FACE,{"disambiguationData":[TD([[makeQuery(id+"F29.imprint","IMPRINT",EDGE,{"derivedFrom":sQuery(id+"F29.wireOp",EDGE,"E25.bottom")}),-1.0]])]});
            extrude(context, id + "F30", {"entities" : qUnion([Q0]), "operationType" : NewBodyOperationType.ADD, "depth" : 39.2 * mm});
        }
        {
            var Q0;
            Q0=makeQuery(id+"F28.opExtrude","SWEPT_EDGE",EDGE,{"disambiguationData":[OSD([sQuery(id+"F27.wireOp",EDGE,"E23.bottom"),sQuery(id+"F27.wireOp",EDGE,"E23.left")])]});
            var Q1;
            Q1=makeQuery(id+"F28.opExtrude","SWEPT_EDGE",EDGE,{"disambiguationData":[OSD([sQuery(id+"F27.wireOp",EDGE,"E23.bottom"),sQuery(id+"F27.wireOp",EDGE,"E23.right")])]});
            chamfer(context, id + "F31", {"entities" : qUnion([Q0, Q1]), "width" : 7 * mm, "tangentPropagation" : true});
        }
        {
            var Q0;
            Q0=makeQuery(id+"F30.boolean.opBoolean","MERGE",FACE,{"derivedFrom":[makeQuery(id+"F28.opExtrude","SWEPT_FACE",FACE,{"disambiguationData":[OSD([sQuery(id+"F27.wireOp",EDGE,"E23.left")])]}),makeQuery(id+"F30.opExtrude","SWEPT_FACE",FACE,{"disambiguationData":[OSD([sQuery(id+"F29.wireOp",EDGE,"E25.right")])]})]});
            var sketch = newSketch(context, id + "F32", { "sketchPlane" : qUnion([Q0])});
            skLineSegment(sketch, "E26", {"start": v(30.2, -13.15) * mm, "end": v(15.2, -28.15) * mm});
            skLineSegment(sketch, "E27", {"start": v(15.2, -28.15) * mm, "end": v(30.2, -28.15) * mm});
            skLineSegment(sketch, "E28", {"start": v(30.2, -28.15) * mm, "end": v(30.2, -13.15) * mm});
            skSolve(sketch);
        }
        {
            var Q0;
            Q0=makeQuery(id+"F32.imprint","IMPRINT",FACE,{"disambiguationData":[TD([[makeQuery(id+"F32.imprint","IMPRINT",EDGE,{"derivedFrom":sQuery(id+"F32.wireOp",EDGE,"E26")}),1.0]])]});
            extrude(context, id + "F33", {"entities" : qUnion([Q0]), "operationType" : NewBodyOperationType.ADD, "oppositeDirection" : true, "depth" : 3 * mm});
        }
        {
            var Q0;
            Q0=makeQuery(id+"F30.boolean.opBoolean","MERGE",FACE,{"derivedFrom":[makeQuery(id+"F28.opExtrude","SWEPT_FACE",FACE,{"disambiguationData":[OSD([sQuery(id+"F27.wireOp",EDGE,"E23.right")])]}),makeQuery(id+"F30.opExtrude","SWEPT_FACE",FACE,{"disambiguationData":[OSD([sQuery(id+"F29.wireOp",EDGE,"E25.left")])]})]});
            var sketch = newSketch(context, id + "F34", { "sketchPlane" : qUnion([Q0])});
            skLineSegment(sketch, "E29", {"start": v(-32.2, -31.15) * mm, "end": v(-17.2, -31.15) * mm});
            skLineSegment(sketch, "E30", {"start": v(-17.2, -31.15) * mm, "end": v(-32.2, -16.15) * mm});
            skLineSegment(sketch, "E31", {"start": v(-32.2, -16.15) * mm, "end": v(-32.2, -31.15) * mm});
            skSolve(sketch);
        }
        {
            var Q0;
            {var subQ0=sQuery(id+"F34.wireOp",EDGE,"E30");var subQ1=sQuery(id+"F27.wireOp",EDGE,"E23.right");var subQ4=makeQuery(id+"F28.opExtrude","CAP_EDGE",EDGE,{"disambiguationData":[OSD([subQ1])],"isStart":true});var subQ5=makeQuery(id+"F34.imprint","INTERSECT",VERTEX,{"derivedFrom":[subQ4,subQ0]});Q0=makeQuery(id+"F34.imprint","IMPRINT",FACE,{"disambiguationData":[TD([[makeQuery(id+"F34.imprint","IMPRINT",EDGE,{"disambiguationData":[TD([[subQ5,1.0]])],"derivedFrom":subQ0}),1.0]])]});}
            var Q1;
            {var subQ5=sQuery(id+"F34.wireOp",EDGE,"E29");Q1=makeQuery(id+"F34.imprint","IMPRINT",FACE,{"disambiguationData":[TD([[makeQuery(id+"F34.imprint","IMPRINT",EDGE,{"derivedFrom":subQ5}),1.0]])]});}
            extrude(context, id + "F35", {"entities" : qUnion([Q0, Q1]), "operationType" : NewBodyOperationType.ADD, "oppositeDirection" : true, "depth" : 3 * mm});
        }
        {
            var Q0;
            Q0=makeQuery(id+"F30.boolean.opBoolean","MERGE",FACE,{"derivedFrom":[makeQuery(id+"F28.opExtrude","SWEPT_FACE",FACE,{"disambiguationData":[OSD([sQuery(id+"F27.wireOp",EDGE,"E23.top")])]}),makeQuery(id+"F30.opExtrude","SWEPT_FACE",FACE,{"disambiguationData":[OSD([sQuery(id+"F29.wireOp",EDGE,"E25.bottom")])]})]});
            var sketch = newSketch(context, id + "F36", { "sketchPlane" : qUnion([Q0])});
            skCircle(sketch, "E32", {"center": v(-20, 3.4) * mm, "radius": 2 * mm});
            skCircle(sketch, "E33", {"center": v(-20, -26.6) * mm, "radius": 2 * mm});
            skCircle(sketch, "E34", {"center": v(20, 3.4) * mm, "radius": 2 * mm});
            skCircle(sketch, "E35", {"center": v(20, -26.6) * mm, "radius": 2 * mm});
            skSolve(sketch);
        }
        {
            var Q0;
            Q0=makeQuery(id+"F36.imprint","IMPRINT",FACE,{"disambiguationData":[TD([[makeQuery(id+"F36.imprint","IMPRINT",EDGE,{"derivedFrom":sQuery(id+"F36.wireOp",EDGE,"E32")}),1.0]])]});
            var Q1;
            Q1=makeQuery(id+"F36.imprint","IMPRINT",FACE,{"disambiguationData":[TD([[makeQuery(id+"F36.imprint","IMPRINT",EDGE,{"derivedFrom":sQuery(id+"F36.wireOp",EDGE,"E33")}),1.0]])]});
            var Q2;
            Q2=makeQuery(id+"F36.imprint","IMPRINT",FACE,{"disambiguationData":[TD([[makeQuery(id+"F36.imprint","IMPRINT",EDGE,{"derivedFrom":sQuery(id+"F36.wireOp",EDGE,"E35")}),1.0]])]});
            var Q3;
            Q3=makeQuery(id+"F36.imprint","IMPRINT",FACE,{"disambiguationData":[TD([[makeQuery(id+"F36.imprint","IMPRINT",EDGE,{"derivedFrom":sQuery(id+"F36.wireOp",EDGE,"E34")}),1.0]])]});
            extrude(context, id + "F37", {"entities" : qUnion([Q0, Q1, Q2, Q3]), "operationType" : NewBodyOperationType.REMOVE, "oppositeDirection" : true, "depth" : 5 * mm});
        }
        {
            var Q0;
            Q0=makeQuery(id+"F28.opExtrude","CAP_EDGE",EDGE,{"disambiguationData":[OSD([sQuery(id+"F27.wireOp",EDGE,"E23.top")])],"isStart":false});
            fillet(context, id + "F38", {"entities" : qUnion([Q0]), "radius" : 3 * mm, "tangentPropagation" : true, "allowEdgeOverflow" : false});
        }
        {
            var Q0;
            Q0=makeQuery(id+"F1.opExtrude","CAP_FACE",FACE,{"disambiguationData":[OSD([sQuery(id+"F0.wireOp",EDGE,"E0.bottom"),sQuery(id+"F0.wireOp",EDGE,"E0.top"),sQuery(id+"F0.wireOp",EDGE,"E0.left"),sQuery(id+"F0.wireOp",EDGE,"E0.right")])],"isStart":false});
            var sketch = newSketch(context, id + "F39", { "sketchPlane" : qUnion([Q0])});
            skCircle(sketch, "E36", {"center": v(0, 0) * mm, "radius": 4.75 * mm});
            skSolve(sketch);
        }
        {
            var Q0;
            Q0=makeQuery(id+"F39.imprint","IMPRINT",FACE,{"disambiguationData":[TD([[makeQuery(id+"F39.imprint","IMPRINT",EDGE,{"derivedFrom":sQuery(id+"F39.wireOp",EDGE,"E36")}),1.0]])]});
            extrude(context, id + "F40", {"entities" : qUnion([Q0]), "operationType" : NewBodyOperationType.REMOVE, "oppositeDirection" : true, "depth" : 4 * mm});
        }
        {
            var Q0;
            Q0=qCreatedBy(makeId("Front.planeOp"),FACE);
            var sketch = newSketch(context, id + "F41", { "sketchPlane" : qUnion([Q0])});
            skCircle(sketch, "E37", {"center": v(-45.42, -7.1) * mm, "radius": 2.5 * mm});
            skSolve(sketch);
        }
        {
            var Q0;
            Q0=makeQuery(id+"F41.imprint","IMPRINT",FACE,{"disambiguationData":[TD([[makeQuery(id+"F41.imprint","IMPRINT",EDGE,{"derivedFrom":sQuery(id+"F41.wireOp",EDGE,"E37")}),1.0]])]});
            extrude(context, id + "F42", {"entities" : qUnion([Q0]), "oppositeDirection" : true, "depth" : 28 * mm});
        }
    });
